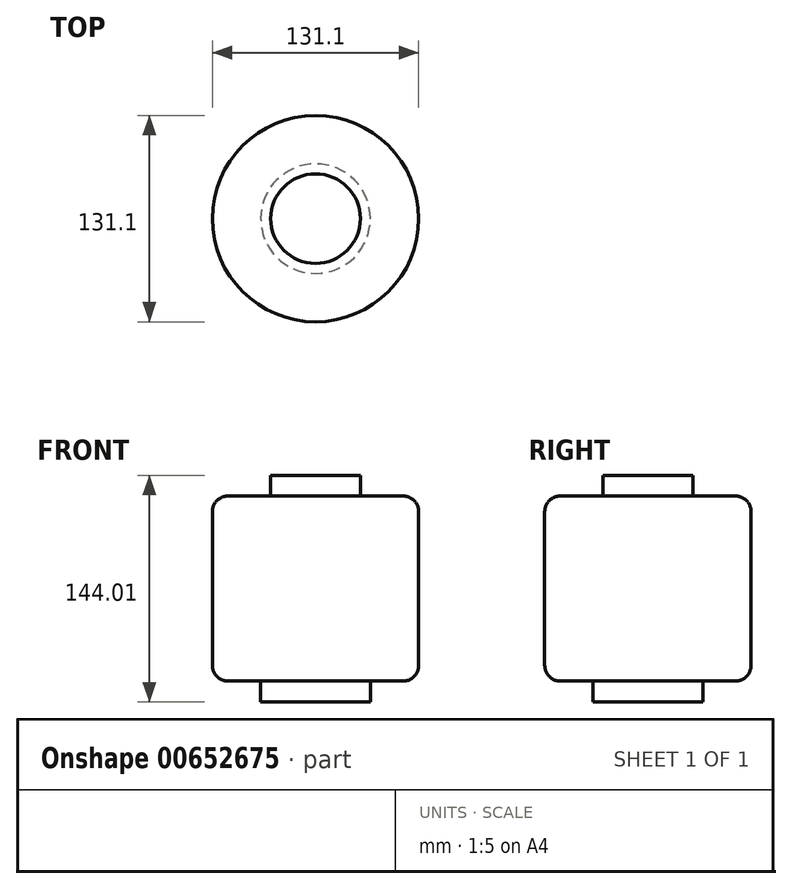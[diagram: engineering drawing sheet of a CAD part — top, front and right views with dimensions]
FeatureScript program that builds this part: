
annotation { "Feature Type Name" : "Feature", "Feature Type Description" : "" }
export const myFeature = defineFeature(function(context is Context, id is Id, definition is map)
    precondition{}
    {
        {
            var Q0;
            Q0=qCreatedBy(makeId("Front.planeOp"),FACE);
            var sketch = newSketch(context, id + "F0", { "sketchPlane" : qUnion([Q0])});
            skPoint(sketch, "E0.middle", {"position": v(0, 0) * mm});
            skPoint(sketch, "E1.middle", {"position": v(0, 58.8) * mm});
            skPoint(sketch, "E2.middle", {"position": v(0, -58.8) * mm});
            skLineSegment(sketch, "E3.bottom", {"start": v(0, 71.9) * mm, "end": v(-28.45, 71.9) * mm});
            skLineSegment(sketch, "E3.top", {"start": v(0, 58.8) * mm, "end": v(-28.45, 58.8) * mm});
            skLineSegment(sketch, "E3.left", {"start": v(0, 71.9) * mm, "end": v(0, 58.8) * mm});
            skLineSegment(sketch, "E3.right", {"start": v(-28.45, 71.9) * mm, "end": v(-28.45, 58.8) * mm});
            skLineSegment(sketch, "E4.bottom", {"start": v(0, -58.8) * mm, "end": v(-34.8, -58.8) * mm});
            skLineSegment(sketch, "E4.top", {"start": v(0, -72.12) * mm, "end": v(-34.8, -72.12) * mm});
            skLineSegment(sketch, "E4.left", {"start": v(0, -58.8) * mm, "end": v(0, -72.12) * mm});
            skLineSegment(sketch, "E4.right", {"start": v(-34.8, -58.8) * mm, "end": v(-34.8, -72.12) * mm});
            skLineSegment(sketch, "E5.bottom", {"start": v(-65.55, 58.8) * mm, "end": v(0, 58.8) * mm});
            skLineSegment(sketch, "E5.top", {"start": v(-65.55, -58.8) * mm, "end": v(0, -58.8) * mm});
            skLineSegment(sketch, "E5.left", {"start": v(-65.55, 58.8) * mm, "end": v(-65.55, -58.8) * mm});
            skLineSegment(sketch, "E5.right", {"start": v(0, 58.8) * mm, "end": v(0, -58.8) * mm});
            skSolve(sketch);
        }
        {
            var Q0;
            Q0=makeQuery(id+"F0.imprint","IMPRINT",FACE,{"disambiguationData":[TD([[makeQuery(id+"F0.imprint","IMPRINT",EDGE,{"derivedFrom":sQuery(id+"F0.wireOp",EDGE,"E3.bottom")}),1.0]])]});
            var Q1;
            {var subQ3=sQuery(id+"F0.wireOp",EDGE,"E5.left");Q1=makeQuery(id+"F0.imprint","IMPRINT",FACE,{"disambiguationData":[TD([[makeQuery(id+"F0.imprint","IMPRINT",EDGE,{"derivedFrom":subQ3}),1.0]])]});}
            var Q2;
            Q2=makeQuery(id+"F0.imprint","IMPRINT",FACE,{"disambiguationData":[TD([[makeQuery(id+"F0.imprint","IMPRINT",EDGE,{"derivedFrom":sQuery(id+"F0.wireOp",EDGE,"E4.top")}),-1.0]])]});
            var Q3;
            Q3=sQuery(id+"F0.wireOp",EDGE,"E5.right");
            revolve(context, id + "F1", {"entities" : qUnion([Q0, Q1, Q2]), "axis" : qUnion([Q3]), "revolveType" : RevolveType.FULL});
        }
        {
            var Q0;
            Q0=makeQuery(id+"F1.opRevolve","SWEPT_FACE",FACE,{"disambiguationData":[OSD([sQuery(id+"F0.wireOp",EDGE,"E5.left")])]});
            fillet(context, id + "F2", {"entities" : qUnion([Q0]), "radius" : 10 * mm, "tangentPropagation" : true, "allowEdgeOverflow" : false});
        }
    });
